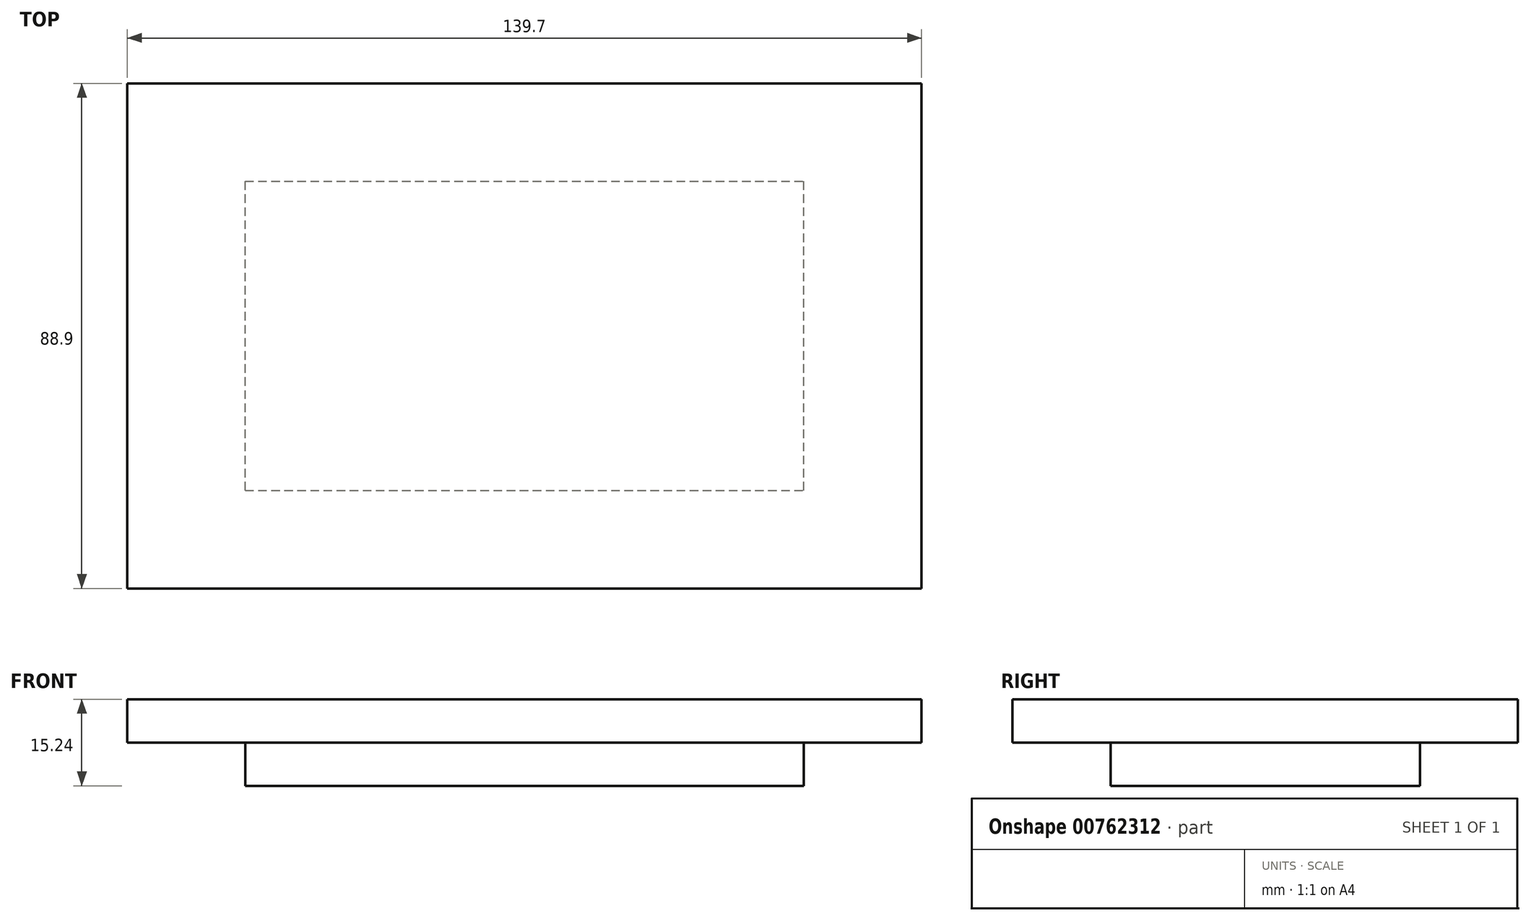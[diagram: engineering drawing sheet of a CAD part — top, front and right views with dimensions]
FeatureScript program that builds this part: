
annotation { "Feature Type Name" : "Feature", "Feature Type Description" : "" }
export const myFeature = defineFeature(function(context is Context, id is Id, definition is map)
    precondition{}
    {
        {
            var Q0;
            Q0=qCreatedBy(makeId("Top.planeOp"),FACE);
            var sketch = newSketch(context, id + "F0", { "sketchPlane" : qUnion([Q0])});
            skLineSegment(sketch, "E0.bottom", {"start": v(-69.85, 44.45) * mm, "end": v(69.85, 44.45) * mm});
            skLineSegment(sketch, "E0.top", {"start": v(-69.85, -44.45) * mm, "end": v(69.85, -44.45) * mm});
            skLineSegment(sketch, "E0.left", {"start": v(-69.85, 44.45) * mm, "end": v(-69.85, -44.45) * mm});
            skLineSegment(sketch, "E0.right", {"start": v(69.85, 44.45) * mm, "end": v(69.85, -44.45) * mm});
            skPoint(sketch, "E0.middle", {"position": v(0, 0) * mm});
            skSolve(sketch);
        }
        {
            var Q0;
            Q0=makeQuery(id+"F0.imprint","IMPRINT",FACE,{"disambiguationData":[TD([[makeQuery(id+"F0.imprint","IMPRINT",EDGE,{"derivedFrom":sQuery(id+"F0.wireOp",EDGE,"E0.bottom")}),-1.0]])]});
            extrude(context, id + "F1", {"entities" : qUnion([Q0]), "depth" : 7.62 * mm, "offsetDistance" : 25.4 * mm});
        }
        {
            var Q0;
            Q0=makeQuery(id+"F1.opExtrude","CAP_FACE",FACE,{"disambiguationData":[OSD([sQuery(id+"F0.wireOp",EDGE,"E0.bottom"),sQuery(id+"F0.wireOp",EDGE,"E0.top"),sQuery(id+"F0.wireOp",EDGE,"E0.left"),sQuery(id+"F0.wireOp",EDGE,"E0.right")])],"isStart":true});
            var sketch = newSketch(context, id + "F2", { "sketchPlane" : qUnion([Q0])});
            skLineSegment(sketch, "E1.bottom", {"start": v(-49.13, 27.2) * mm, "end": v(49.13, 27.2) * mm});
            skLineSegment(sketch, "E1.top", {"start": v(-49.13, -27.2) * mm, "end": v(49.13, -27.2) * mm});
            skLineSegment(sketch, "E1.left", {"start": v(-49.13, 27.2) * mm, "end": v(-49.13, -27.2) * mm});
            skLineSegment(sketch, "E1.right", {"start": v(49.13, 27.2) * mm, "end": v(49.13, -27.2) * mm});
            skPoint(sketch, "E1.middle", {"position": v(0, 0) * mm});
            skSolve(sketch);
        }
        {
            var Q0;
            Q0=makeQuery(id+"F2.imprint","IMPRINT",FACE,{"disambiguationData":[TD([[makeQuery(id+"F2.imprint","IMPRINT",EDGE,{"derivedFrom":sQuery(id+"F2.wireOp",EDGE,"E1.bottom")}),-1.0]])]});
            extrude(context, id + "F3", {"entities" : qUnion([Q0]), "depth" : 7.62 * mm, "offsetDistance" : 25.4 * mm});
        }
    });
